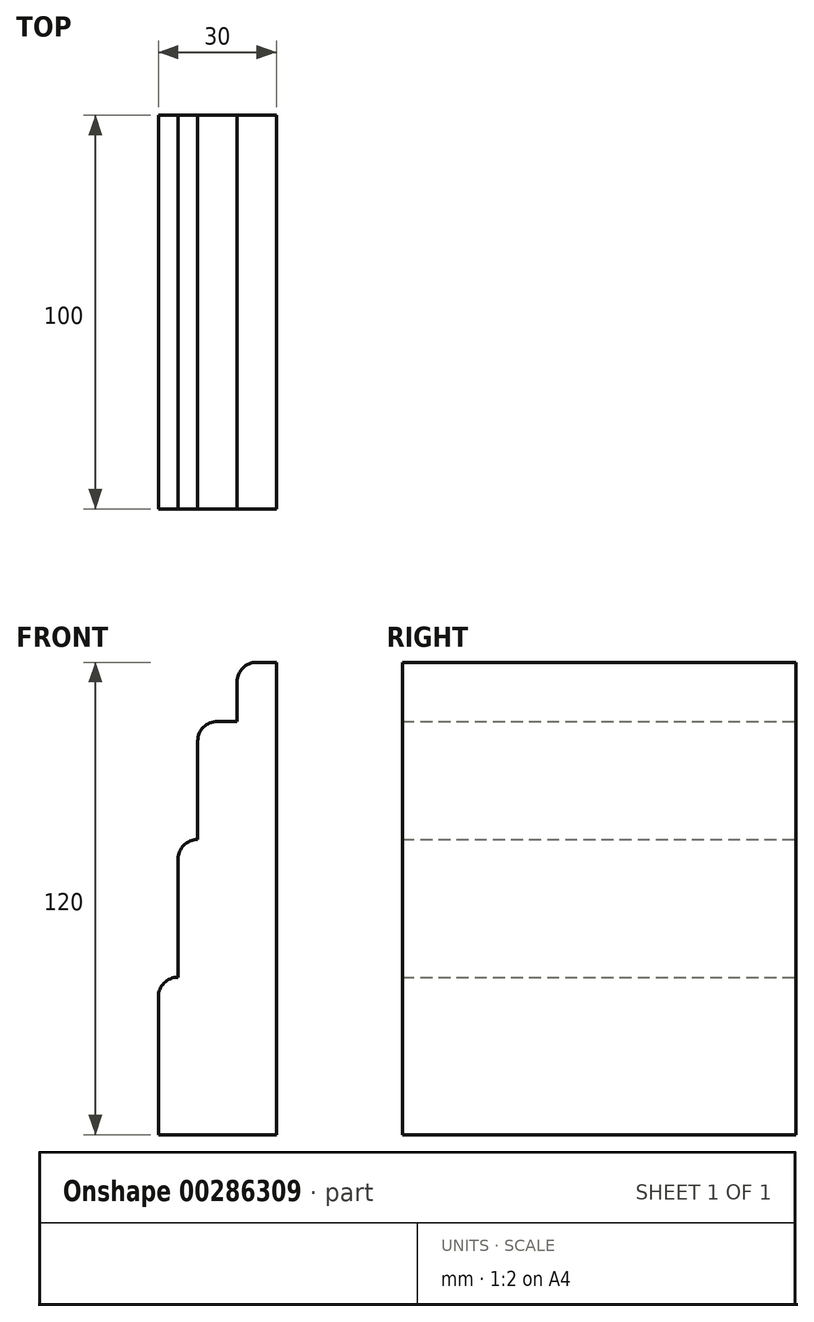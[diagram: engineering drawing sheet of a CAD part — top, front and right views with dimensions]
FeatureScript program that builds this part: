
annotation { "Feature Type Name" : "Feature", "Feature Type Description" : "" }
export const myFeature = defineFeature(function(context is Context, id is Id, definition is map)
    precondition{}
    {
        {
            var Q0;
            Q0=qCreatedBy(makeId("Front.planeOp"),FACE);
            var sketch = newSketch(context, id + "F0", { "sketchPlane" : qUnion([Q0])});
            skLineSegment(sketch, "E0", {"start": v(34.87, 67.16) * mm, "end": v(34.87, -52.84) * mm});
            skLineSegment(sketch, "E1", {"start": v(34.87, -52.84) * mm, "end": v(4.87, -52.84) * mm});
            skLineSegment(sketch, "E2", {"start": v(4.87, -52.84) * mm, "end": v(4.87, -17.84) * mm});
            skLineSegment(sketch, "E3", {"start": v(9.87, -12.84) * mm, "end": v(9.87, -12.84) * mm});
            skLineSegment(sketch, "E4", {"start": v(9.87, -12.84) * mm, "end": v(9.87, 17.16) * mm});
            skLineSegment(sketch, "E5", {"start": v(14.87, 22.16) * mm, "end": v(14.87, 22.16) * mm});
            skLineSegment(sketch, "E6", {"start": v(14.87, 22.16) * mm, "end": v(14.87, 47.16) * mm});
            skLineSegment(sketch, "E7", {"start": v(19.87, 52.16) * mm, "end": v(24.87, 52.16) * mm});
            skLineSegment(sketch, "E8", {"start": v(24.87, 52.16) * mm, "end": v(24.87, 62.16) * mm});
            skLineSegment(sketch, "E9", {"start": v(29.87, 67.16) * mm, "end": v(34.87, 67.16) * mm});
            skPoint(sketch, "E10.visualSharp", {"position": v(4.87, -12.84) * mm});
            skArc(sketch, "E10.filletArc", {"start": v(9.87, -12.84) * mm, "mid": v(6.33, -14.3) * mm, "end": v(4.87, -17.84) * mm});
            skPoint(sketch, "E11.visualSharp", {"position": v(9.87, 22.16) * mm});
            skArc(sketch, "E11.filletArc", {"start": v(14.87, 22.16) * mm, "mid": v(11.33, 20.7) * mm, "end": v(9.87, 17.16) * mm});
            skPoint(sketch, "E12.visualSharp", {"position": v(14.87, 52.16) * mm});
            skArc(sketch, "E12.filletArc", {"start": v(19.87, 52.16) * mm, "mid": v(16.33, 50.7) * mm, "end": v(14.87, 47.16) * mm});
            skPoint(sketch, "E13.visualSharp", {"position": v(24.87, 67.16) * mm});
            skArc(sketch, "E13.filletArc", {"start": v(29.87, 67.16) * mm, "mid": v(26.33, 65.7) * mm, "end": v(24.87, 62.16) * mm});
            skSolve(sketch);
        }
        {
            var Q0;
            Q0=makeQuery(id+"F0.imprint","IMPRINT",FACE,{"disambiguationData":[TD([[makeQuery(id+"F0.imprint","IMPRINT",EDGE,{"derivedFrom":sQuery(id+"F0.wireOp",EDGE,"E0")}),-1.0]])]});
            extrude(context, id + "F1", {"entities" : qUnion([Q0]), "depth" : 100 * mm});
        }
    });
